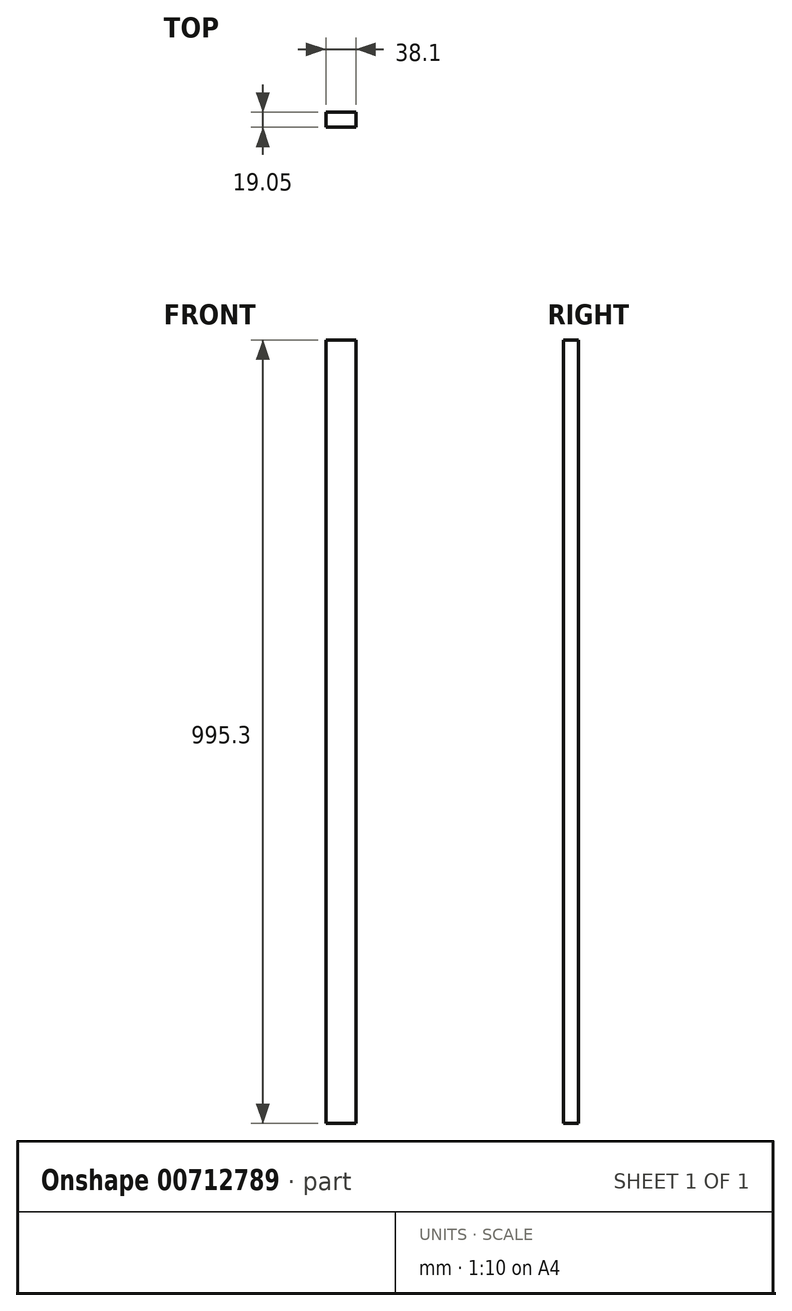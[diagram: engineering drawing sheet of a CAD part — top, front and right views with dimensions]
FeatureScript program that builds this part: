
annotation { "Feature Type Name" : "Feature", "Feature Type Description" : "" }
export const myFeature = defineFeature(function(context is Context, id is Id, definition is map)
    precondition{}
    {
        {
            var Q0;
            Q0=qCreatedBy(makeId("Top.planeOp"),FACE);
            var sketch = newSketch(context, id + "F0", { "sketchPlane" : qUnion([Q0])});
            skLineSegment(sketch, "E0.bottom", {"start": v(0, 0) * mm, "end": v(-38.1, 0) * mm});
            skLineSegment(sketch, "E0.top", {"start": v(0, 19.05) * mm, "end": v(-38.1, 19.05) * mm});
            skLineSegment(sketch, "E0.left", {"start": v(0, 0) * mm, "end": v(0, 19.05) * mm});
            skLineSegment(sketch, "E0.right", {"start": v(-38.1, 0) * mm, "end": v(-38.1, 19.05) * mm});
            skSolve(sketch);
        }
        {
            var Q0;
            Q0 = qSketchRegion(id + "F0", true);
            extrude(context, id + "F1", {"entities" : qUnion([Q0]), "depth" : 995.3 * mm, "offsetDistance" : 25.4 * mm});
        }
    });
